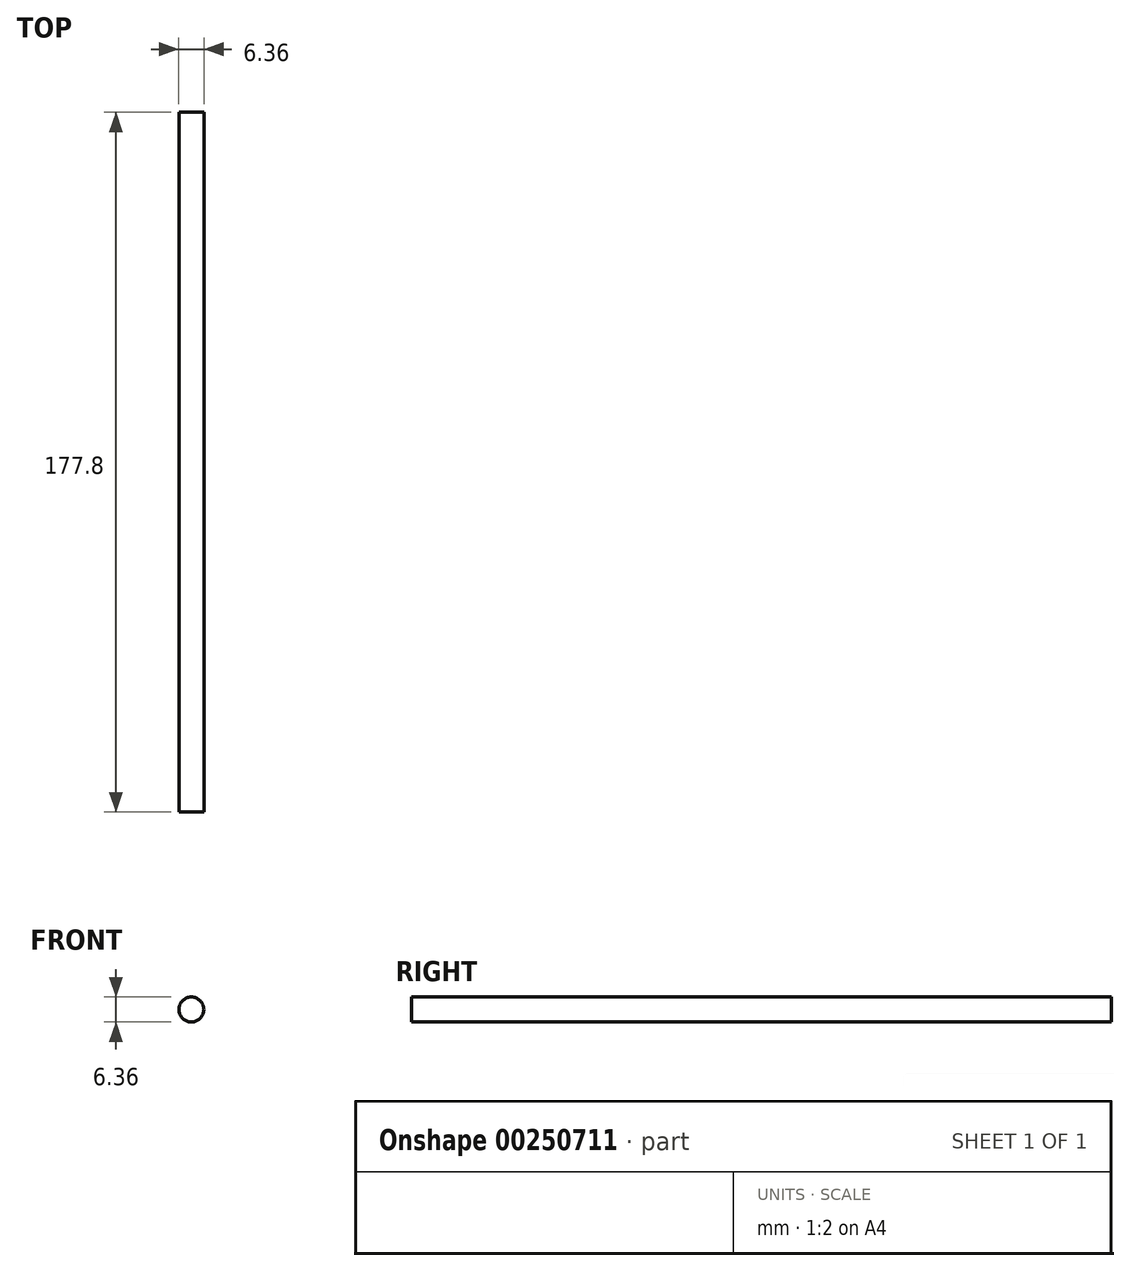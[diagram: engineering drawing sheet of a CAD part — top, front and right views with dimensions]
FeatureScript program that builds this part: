
annotation { "Feature Type Name" : "Feature", "Feature Type Description" : "" }
export const myFeature = defineFeature(function(context is Context, id is Id, definition is map)
    precondition{}
    {
        {
            var Q0;
            Q0=qCreatedBy(makeId("Front.planeOp"),FACE);
            var sketch = newSketch(context, id + "F0", { "sketchPlane" : qUnion([Q0])});
            skCircle(sketch, "E0", {"center": v(0, 0) * mm, "radius": 3.17 * mm});
            skSolve(sketch);
        }
        {
            var Q0;
            Q0=makeQuery(id+"F0.imprint","IMPRINT",FACE,{"disambiguationData":[TD([[makeQuery(id+"F0.imprint","IMPRINT",EDGE,{"derivedFrom":sQuery(id+"F0.wireOp",EDGE,"E0")}),1.0]])]});
            extrude(context, id + "F1", {"entities" : qUnion([Q0]), "depth" : 177.8 * mm});
        }
    });
